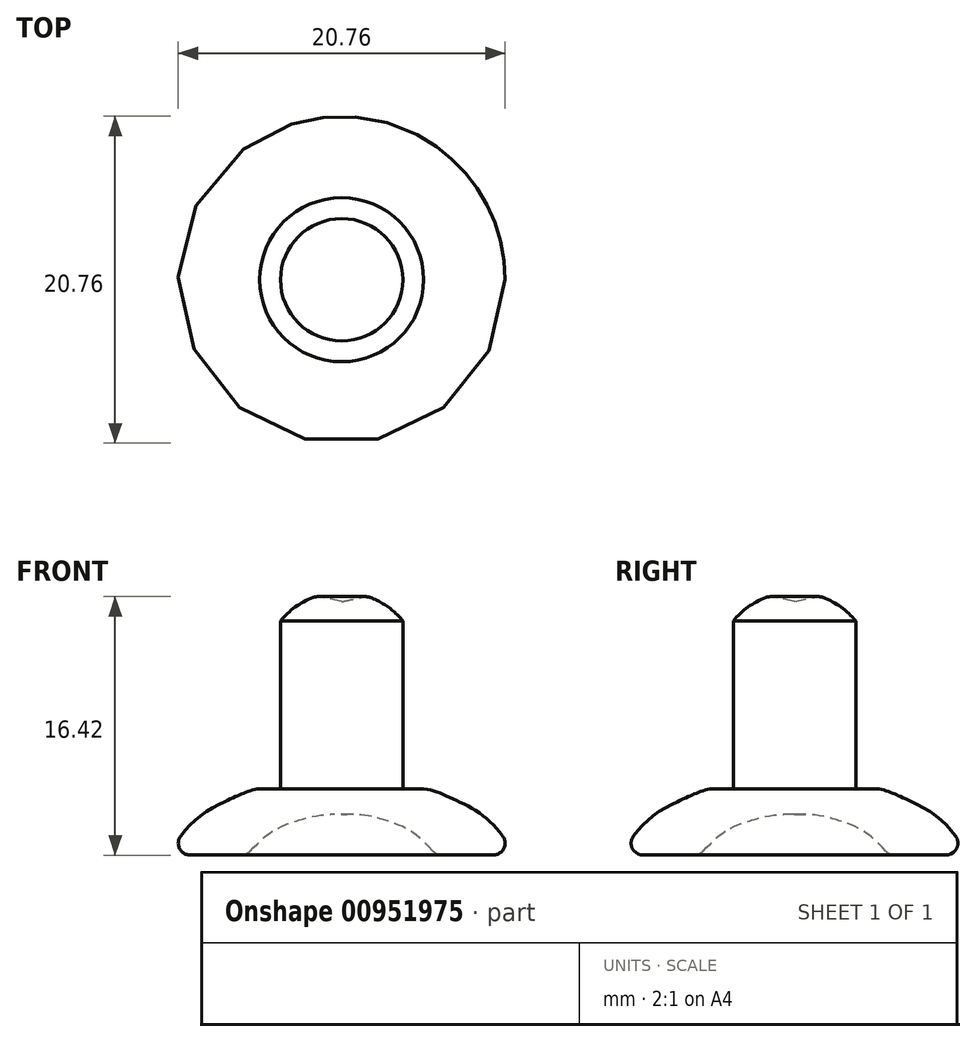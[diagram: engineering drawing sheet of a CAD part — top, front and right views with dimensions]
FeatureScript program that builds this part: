
annotation { "Feature Type Name" : "Feature", "Feature Type Description" : "" }
export const myFeature = defineFeature(function(context is Context, id is Id, definition is map)
    precondition{}
    {
        {
            var Q0;
            Q0=qCreatedBy(makeId("Front.planeOp"),FACE);
            var sketch = newSketch(context, id + "F0", { "sketchPlane" : qUnion([Q0])});
            skLineSegment(sketch, "E0", {"start": v(3.89, 11.7) * mm, "end": v(3.89, 1.04) * mm});
            skLineSegment(sketch, "E1", {"start": v(11.11, -3.18) * mm, "end": v(6.03, -3.18) * mm});
            skFitSpline(sketch, "E2", {"points": [v(6.03, -3.18) * mm, v(3.78, -1.33) * mm, v(2.1, -0.78) * mm, v(0, -0.64) * mm], "startDerivative": vector(-8.72, 9.61) * mm, "endDerivative": vector(-8.58, -0.86) * mm});
            skLineSegment(sketch, "E3", {"start": v(3.89, 1.04) * mm, "end": v(5.2, 1.04) * mm});
            skPoint(sketch, "E4.orphan", {"position": v(3.89, 0) * mm});
            skPoint(sketch, "E5.start.orphan", {"position": v(0, 13.53) * mm});
            skArc(sketch, "E6", {"start": v(3.89, 11.7) * mm, "mid": v(2.85, 12.65) * mm, "end": v(1.6, 13.27) * mm});
            skLineSegment(sketch, "E7", {"start": v(1.6, 13.27) * mm, "end": v(0, 12.92) * mm});
            skLineSegment(sketch, "E8", {"start": v(0, 12.92) * mm, "end": v(0, -0.64) * mm});
            skPoint(sketch, "E9.1.internal.snap0", {"position": v(8.16, 0.53) * mm});
            skFitSpline(sketch, "E9", {"points": [v(5.2, 1.04) * mm, v(6.75, 0.53) * mm, v(9.04, -0.72) * mm, v(11.11, -3.17) * mm], "startDerivative": vector(6.51, -0.67) * mm, "endDerivative": vector(5, -7.08) * mm});
            skPoint(sketch, "E10.start.orphan", {"position": v(11.11, 0.02) * mm});
            skSolve(sketch);
        }
        {
            var Q0;
            Q0=qCreatedBy(makeId("Front.planeOp"),FACE);
            var sketch = newSketch(context, id + "F1", { "sketchPlane" : qUnion([Q0])});
            skLineSegment(sketch, "E11", {"start": v(0, 15.07) * mm, "end": v(0, -12.26) * mm});
            skSolve(sketch);
        }
        {
            var Q0;
            Q0 = qSketchRegion(id + "F0", true);
            var Q1;
            Q1=sQuery(id+"F1.wireOp",EDGE,"E11");
            revolve(context, id + "F2", {"surfaceOperationType" : NewSurfaceOperationType.NEW, "entities" : qUnion([Q0]), "axis" : qUnion([Q1]), "revolveType" : RevolveType.FULL});
        }
        {
            var Q0;
            Q0=makeQuery(id+"F2.opRevolve","SWEPT_EDGE",EDGE,{"disambiguationData":[OSD([sQuery(id+"F0.wireOp",EDGE,"E10"),sQuery(id+"F0.wireOp",EDGE,"E1")])]});
            var Q1;
            Q1=makeQuery(id+"F2.opRevolve","SWEPT_EDGE",EDGE,{"disambiguationData":[OSD([sQuery(id+"F0.wireOp",EDGE,"87Vvx1ou-ejO2-N0P8-hX72-8iQDBueiMVd5"),sQuery(id+"F0.wireOp",EDGE,"E10")])]});
            var Q2;
            Q2=makeQuery(id+"F2.opRevolve","SWEPT_EDGE",EDGE,{"disambiguationData":[OSD([sQuery(id+"F0.wireOp",EDGE,"E6"),sQuery(id+"F0.wireOp",EDGE,"E7")])]});
            fillet(context, id + "F3", {"entities" : qUnion([Q0, Q1, Q2]), "radius" : 0.76 * mm, "tangentPropagation" : true, "allowEdgeOverflow" : false});
        }
    });
